# Revit family: RN 90046 Optifitt-Serra-Nippel doppio ridotto
name_source: partatom
category: Rohrformteile
units: mm (PartAtom-declared; Revit-internal decimal feet)

## family parameters
Arbeitsebenenbasiert = Nein
Beim Laden mit Abzugskörper schneiden = Nein
Bemaßung runder Anschluss = Durchmesser verwenden
Gemeinsam genutzt = Nein
Immer vertikal = Ja
Teiletyp = Nicht definiert

## types (10) — shared parameters
1.010.00.2 Blattnummer der Richtlinie = 29
1.010.00.3 Ausgabedatum (Monat) der Richtlinie = 201308
1.010.00.4 Herstellername = R. Nussbaum AG
1.010.00.5 Revisionsdatum der Datei = 20190521
1.010.00.6 Webadresse des Herstellers = http://www.nussbaum.ch
1.100.00.4 Produktbezeichnung = Versorgung
1.110.00.2 Index = 3
1.110.00.4 Produktbezeichnung = Optifitt-Serra
1.960/3L.00.8 Link (URL) = https://www.nussbaum.ch
29.700.00.4 Produktname = Optifitt-Serra-Doppelnippel reduziert, für flachdichtende Verschraubungen
29.700.00.5 Produktkennung = 2
29.700.00.6 Querschnittsform = 1
29.700.00.7 Nennweitensystem = DN
29.700.00.8 Nenndrucksystem = PN
29.710.02.4 Nenndruck = 16
29.710.02.5 max. zul. Überdruck [hPa] = 1600
29.710.02.7 max. zul. Dauer-Betriebsdruck [hPa] = 1600
29.710.02.9 max. zul. Dauer-Betriebstemperatur [°C] = 90
Connector Visibility = Nein
EnclosingSpace Visibility = Nein
Hersteller = R. Nussbaum AG
URL = https://www.nussbaum.ch

## per-type parameters (varying)
- DN=12x15: 1.800.00.3 TGA-Nummer=01900300000000000000000000000000000000000000000026000000000000000010; 1.800.00.4 Kommentarfeld=90046.20, Optifitt-Serra-Doppelnippel reduziert, für flachdichtende Verschraubungen, DN=12x15, L=25, R=3/8; 1.810.00.3 Hersteller-Bestellnummer=90046.2; 1.810.00.4 DATANORM-Nummer=90046.2; 1.810.00.6 GTIN-Nummer=7612945723567; 29.710.02.10 Formstück-Gewicht [kg]=0.044; 29.710.02.3 Benennung=Optifitt-Serra-Doppelnippel reduziert, für flachdichtende Verschraubungen, DN=12x15, L=25, R=3/8; CONNECTOR0_DIAMETER_dX_0r=10 mm  [stored 0.0328084 ft]; CONNECTOR0_dX_01=10 mm  [stored 0.0328084 ft]; CONNECTOR0_ref_dX=10 mm  [stored 0.0328084 ft]; CONNECTOR1_DIAMETER_dX_0r=15 mm; CONNECTOR1_dX_00=15 mm; CONNECTOR1_dX_01=24 mm; CONNECTOR1_ref_dX=15 mm; CONNECTOR1_ref_dX2=24 mm; Modell=90046.2; R. Nussbaum AG 90046.20 de Visibility=Ja; R. Nussbaum AG 90046.21 de Visibility=Nein; R. Nussbaum AG 90046.22 de Visibility=Nein; R. Nussbaum AG 90046.23 de Visibility=Nein; R. Nussbaum AG 90046.24 de Visibility=Nein; R. Nussbaum AG 90046.25 de Visibility=Nein; R. Nussbaum AG 90046.26 de Visibility=Nein; R. Nussbaum AG 90046.27 de Visibility=Nein; R. Nussbaum AG 90046.29 de Visibility=Nein; R. Nussbaum AG 90046.31 de Visibility=Nein; Typenkommentare=Optifitt-Serra-Nippel doppio ridotto  DN=12x15
- DN=40x50: 1.800.00.3 TGA-Nummer=01900300000000000000000000000000000000000000000026000000000000000009; 1.800.00.4 Kommentarfeld=90046.31, Optifitt-Serra-Doppelnippel reduziert, für flachdichtende Verschraubungen, DN=40x50, L=49, R=1½; 1.810.00.3 Hersteller-Bestellnummer=90046.31; 1.810.00.4 DATANORM-Nummer=90046.31; 1.810.00.6 GTIN-Nummer=7612945723604; 29.710.02.10 Formstück-Gewicht [kg]=0.424; 29.710.02.3 Benennung=Optifitt-Serra-Doppelnippel reduziert, für flachdichtende Verschraubungen, DN=40x50, L=49, R=1½; CONNECTOR0_DIAMETER_dX_0r=40 mm; CONNECTOR0_dX_01=19 mm; CONNECTOR0_ref_dX=19 mm; CONNECTOR1_DIAMETER_dX_0r=50 mm; CONNECTOR1_dX_00=33 mm; CONNECTOR1_dX_01=49 mm; CONNECTOR1_ref_dX=33 mm; CONNECTOR1_ref_dX2=49 mm; Modell=90046.31; R. Nussbaum AG 90046.20 de Visibility=Nein; R. Nussbaum AG 90046.21 de Visibility=Nein; R. Nussbaum AG 90046.22 de Visibility=Nein; R. Nussbaum AG 90046.23 de Visibility=Nein; R. Nussbaum AG 90046.24 de Visibility=Nein; R. Nussbaum AG 90046.25 de Visibility=Nein; R. Nussbaum AG 90046.26 de Visibility=Nein; R. Nussbaum AG 90046.27 de Visibility=Nein; R. Nussbaum AG 90046.29 de Visibility=Nein; R. Nussbaum AG 90046.31 de Visibility=Ja; Typenkommentare=Optifitt-Serra-Nippel doppio ridotto  DN=40x50
- DN=15x25: 1.800.00.3 TGA-Nummer=01900300000000000000000000000000000000000000000026000000000000000008; 1.800.00.4 Kommentarfeld=90046.29, Optifitt-Serra-Doppelnippel reduziert, für flachdichtende Verschraubungen, DN=15x25, L=30, R=½; 1.810.00.3 Hersteller-Bestellnummer=90046.29; 1.810.00.4 DATANORM-Nummer=90046.29; 1.810.00.6 GTIN-Nummer=7612945723581; 29.710.02.10 Formstück-Gewicht [kg]=0.084; 29.710.02.3 Benennung=Optifitt-Serra-Doppelnippel reduziert, für flachdichtende Verschraubungen, DN=15x25, L=30, R=½; CONNECTOR0_DIAMETER_dX_0r=15 mm; CONNECTOR0_dX_01=13 mm; CONNECTOR0_ref_dX=13 mm; CONNECTOR1_DIAMETER_dX_0r=25 mm  [stored 0.082021 ft]; CONNECTOR1_dX_00=18 mm; CONNECTOR1_dX_01=30 mm; CONNECTOR1_ref_dX=18 mm; CONNECTOR1_ref_dX2=30 mm; Modell=90046.29; R. Nussbaum AG 90046.20 de Visibility=Nein; R. Nussbaum AG 90046.21 de Visibility=Nein; R. Nussbaum AG 90046.22 de Visibility=Nein; R. Nussbaum AG 90046.23 de Visibility=Nein; R. Nussbaum AG 90046.24 de Visibility=Nein; R. Nussbaum AG 90046.25 de Visibility=Nein; R. Nussbaum AG 90046.26 de Visibility=Nein; R. Nussbaum AG 90046.27 de Visibility=Nein; R. Nussbaum AG 90046.29 de Visibility=Ja; R. Nussbaum AG 90046.31 de Visibility=Nein; Typenkommentare=Optifitt-Serra-Nippel doppio ridotto  DN=15x25
- DN=25: 1.800.00.3 TGA-Nummer=01900300000000000000000000000000000000000000000026000000000000000007; 1.800.00.4 Kommentarfeld=90046.27, Optifitt-Serra-Doppelnippel reduziert, für flachdichtende Verschraubungen, DN=25, L=39, R=1; 1.810.00.3 Hersteller-Bestellnummer=90046.27; 1.810.00.4 DATANORM-Nummer=90046.27; 1.810.00.6 GTIN-Nummer=7612945035219; 29.710.02.10 Formstück-Gewicht [kg]=0.095; 29.710.02.3 Benennung=Optifitt-Serra-Doppelnippel reduziert, für flachdichtende Verschraubungen, DN=25, L=39, R=1; CONNECTOR0_DIAMETER_dX_0r=25 mm  [stored 0.082021 ft]; CONNECTOR0_dX_01=17 mm; CONNECTOR0_ref_dX=17 mm; CONNECTOR1_DIAMETER_dX_0r=25 mm  [stored 0.082021 ft]; CONNECTOR1_dX_00=24 mm; CONNECTOR1_dX_01=36 mm; CONNECTOR1_ref_dX=24 mm; CONNECTOR1_ref_dX2=36 mm; Modell=90046.27; R. Nussbaum AG 90046.20 de Visibility=Nein; R. Nussbaum AG 90046.21 de Visibility=Nein; R. Nussbaum AG 90046.22 de Visibility=Nein; R. Nussbaum AG 90046.23 de Visibility=Nein; R. Nussbaum AG 90046.24 de Visibility=Nein; R. Nussbaum AG 90046.25 de Visibility=Nein; R. Nussbaum AG 90046.26 de Visibility=Nein; R. Nussbaum AG 90046.27 de Visibility=Ja; R. Nussbaum AG 90046.29 de Visibility=Nein; R. Nussbaum AG 90046.31 de Visibility=Nein; Typenkommentare=Optifitt-Serra-Nippel doppio ridotto  DN=25
- DN=20: 1.800.00.3 TGA-Nummer=01900300000000000000000000000000000000000000000026000000000000000006; 1.800.00.4 Kommentarfeld=90046.26, Optifitt-Serra-Doppelnippel reduziert, für flachdichtende Verschraubungen, DN=20, L=33, R=¾; 1.810.00.3 Hersteller-Bestellnummer=90046.26; 1.810.00.4 DATANORM-Nummer=90046.26; 1.810.00.6 GTIN-Nummer=7612945035202; 29.710.02.10 Formstück-Gewicht [kg]=0.059; 29.710.02.3 Benennung=Optifitt-Serra-Doppelnippel reduziert, für flachdichtende Verschraubungen, DN=20, L=33, R=¾; CONNECTOR0_DIAMETER_dX_0r=20 mm; CONNECTOR0_dX_01=15 mm; CONNECTOR0_ref_dX=15 mm; CONNECTOR1_DIAMETER_dX_0r=20 mm; CONNECTOR1_dX_00=21 mm; CONNECTOR1_dX_01=33 mm; CONNECTOR1_ref_dX=21 mm; CONNECTOR1_ref_dX2=33 mm; Modell=90046.26; R. Nussbaum AG 90046.20 de Visibility=Nein; R. Nussbaum AG 90046.21 de Visibility=Nein; R. Nussbaum AG 90046.22 de Visibility=Nein; R. Nussbaum AG 90046.23 de Visibility=Nein; R. Nussbaum AG 90046.24 de Visibility=Nein; R. Nussbaum AG 90046.25 de Visibility=Nein; R. Nussbaum AG 90046.26 de Visibility=Ja; R. Nussbaum AG 90046.27 de Visibility=Nein; R. Nussbaum AG 90046.29 de Visibility=Nein; R. Nussbaum AG 90046.31 de Visibility=Nein; Typenkommentare=Optifitt-Serra-Nippel doppio ridotto  DN=20
- DN=32x40: 1.800.00.3 TGA-Nummer=01900300000000000000000000000000000000000000000026000000000000000005; 1.800.00.4 Kommentarfeld=90046.25, Optifitt-Serra-Doppelnippel reduziert, für flachdichtende Verschraubungen, DN=32x40, L=45, R=1¼; 1.810.00.3 Hersteller-Bestellnummer=90046.25; 1.810.00.4 DATANORM-Nummer=90046.25; 1.810.00.6 GTIN-Nummer=7612945035196; 29.710.02.10 Formstück-Gewicht [kg]=0.214; 29.710.02.3 Benennung=Optifitt-Serra-Doppelnippel reduziert, für flachdichtende Verschraubungen, DN=32x40, L=45, R=1¼; CONNECTOR0_DIAMETER_dX_0r=32 mm; CONNECTOR0_dX_01=19 mm; CONNECTOR0_ref_dX=19 mm; CONNECTOR1_DIAMETER_dX_0r=40 mm; CONNECTOR1_dX_00=31 mm; CONNECTOR1_dX_01=45 mm; CONNECTOR1_ref_dX=31 mm; CONNECTOR1_ref_dX2=45 mm; Modell=90046.25; R. Nussbaum AG 90046.20 de Visibility=Nein; R. Nussbaum AG 90046.21 de Visibility=Nein; R. Nussbaum AG 90046.22 de Visibility=Nein; R. Nussbaum AG 90046.23 de Visibility=Nein; R. Nussbaum AG 90046.24 de Visibility=Nein; R. Nussbaum AG 90046.25 de Visibility=Ja; R. Nussbaum AG 90046.26 de Visibility=Nein; R. Nussbaum AG 90046.27 de Visibility=Nein; R. Nussbaum AG 90046.29 de Visibility=Nein; R. Nussbaum AG 90046.31 de Visibility=Nein; Typenkommentare=Optifitt-Serra-Nippel doppio ridotto  DN=32x40
- DN=25x32: 1.800.00.3 TGA-Nummer=01900300000000000000000000000000000000000000000026000000000000000004; 1.800.00.4 Kommentarfeld=90046.24, Optifitt-Serra-Doppelnippel reduziert, für flachdichtende Verschraubungen, DN=25x32, L=37, R=1; 1.810.00.3 Hersteller-Bestellnummer=90046.24; 1.810.00.4 DATANORM-Nummer=90046.24; 1.810.00.6 GTIN-Nummer=7612945035189; 29.710.02.10 Formstück-Gewicht [kg]=0.135; 29.710.02.3 Benennung=Optifitt-Serra-Doppelnippel reduziert, für flachdichtende Verschraubungen, DN=25x32, L=37, R=1; CONNECTOR0_DIAMETER_dX_0r=25 mm  [stored 0.082021 ft]; CONNECTOR0_dX_01=17 mm; CONNECTOR0_ref_dX=17 mm; CONNECTOR1_DIAMETER_dX_0r=32 mm; CONNECTOR1_dX_00=22 mm; CONNECTOR1_dX_01=36 mm; CONNECTOR1_ref_dX=22 mm; CONNECTOR1_ref_dX2=36 mm; Modell=90046.24; R. Nussbaum AG 90046.20 de Visibility=Nein; R. Nussbaum AG 90046.21 de Visibility=Nein; R. Nussbaum AG 90046.22 de Visibility=Nein; R. Nussbaum AG 90046.23 de Visibility=Nein; R. Nussbaum AG 90046.24 de Visibility=Ja; R. Nussbaum AG 90046.25 de Visibility=Nein; R. Nussbaum AG 90046.26 de Visibility=Nein; R. Nussbaum AG 90046.27 de Visibility=Nein; R. Nussbaum AG 90046.29 de Visibility=Nein; R. Nussbaum AG 90046.31 de Visibility=Nein; Typenkommentare=Optifitt-Serra-Nippel doppio ridotto  DN=25x32
- DN=20x25: 1.800.00.3 TGA-Nummer=01900300000000000000000000000000000000000000000026000000000000000003; 1.800.00.4 Kommentarfeld=90046.23, Optifitt-Serra-Doppelnippel reduziert, für flachdichtende Verschraubungen, DN=20x25, L=35, R=¾; 1.810.00.3 Hersteller-Bestellnummer=90046.23; 1.810.00.4 DATANORM-Nummer=90046.23; 1.810.00.6 GTIN-Nummer=7612945035172; 29.710.02.10 Formstück-Gewicht [kg]=0.089; 29.710.02.3 Benennung=Optifitt-Serra-Doppelnippel reduziert, für flachdichtende Verschraubungen, DN=20x25, L=35, R=¾; CONNECTOR0_DIAMETER_dX_0r=20 mm; CONNECTOR0_dX_01=15 mm; CONNECTOR0_ref_dX=15 mm; CONNECTOR1_DIAMETER_dX_0r=25 mm  [stored 0.082021 ft]; CONNECTOR1_dX_00=21 mm; CONNECTOR1_dX_01=35 mm; CONNECTOR1_ref_dX=21 mm; CONNECTOR1_ref_dX2=35 mm; Modell=90046.23; R. Nussbaum AG 90046.20 de Visibility=Nein; R. Nussbaum AG 90046.21 de Visibility=Nein; R. Nussbaum AG 90046.22 de Visibility=Nein; R. Nussbaum AG 90046.23 de Visibility=Ja; R. Nussbaum AG 90046.24 de Visibility=Nein; R. Nussbaum AG 90046.25 de Visibility=Nein; R. Nussbaum AG 90046.26 de Visibility=Nein; R. Nussbaum AG 90046.27 de Visibility=Nein; R. Nussbaum AG 90046.29 de Visibility=Nein; R. Nussbaum AG 90046.31 de Visibility=Nein; Typenkommentare=Optifitt-Serra-Nippel doppio ridotto  DN=20x25
- DN=15x20: 1.800.00.3 TGA-Nummer=01900300000000000000000000000000000000000000000026000000000000000002; 1.800.00.4 Kommentarfeld=90046.22, Optifitt-Serra-Doppelnippel reduziert, für flachdichtende Verschraubungen, DN=15x20, L=30, R=½; 1.810.00.3 Hersteller-Bestellnummer=90046.22; 1.810.00.4 DATANORM-Nummer=90046.22; 1.810.00.6 GTIN-Nummer=7612945035165; 29.710.02.10 Formstück-Gewicht [kg]=0.052; 29.710.02.3 Benennung=Optifitt-Serra-Doppelnippel reduziert, für flachdichtende Verschraubungen, DN=15x20, L=30, R=½; CONNECTOR0_DIAMETER_dX_0r=15 mm; CONNECTOR0_dX_01=13 mm; CONNECTOR0_ref_dX=13 mm; CONNECTOR1_DIAMETER_dX_0r=20 mm; CONNECTOR1_dX_00=19 mm; CONNECTOR1_dX_01=31 mm; CONNECTOR1_ref_dX=19 mm; CONNECTOR1_ref_dX2=31 mm; Modell=90046.22; R. Nussbaum AG 90046.20 de Visibility=Nein; R. Nussbaum AG 90046.21 de Visibility=Nein; R. Nussbaum AG 90046.22 de Visibility=Ja; R. Nussbaum AG 90046.23 de Visibility=Nein; R. Nussbaum AG 90046.24 de Visibility=Nein; R. Nussbaum AG 90046.25 de Visibility=Nein; R. Nussbaum AG 90046.26 de Visibility=Nein; R. Nussbaum AG 90046.27 de Visibility=Nein; R. Nussbaum AG 90046.29 de Visibility=Nein; R. Nussbaum AG 90046.31 de Visibility=Nein; Typenkommentare=Optifitt-Serra-Nippel doppio ridotto  DN=15x20
- DN=12x20: 1.800.00.3 TGA-Nummer=01900300000000000000000000000000000000000000000026000000000000000001; 1.800.00.4 Kommentarfeld=90046.21, Optifitt-Serra-Doppelnippel reduziert, für flachdichtende Verschraubungen, DN=12x20, L=27, R=3/8; 1.810.00.3 Hersteller-Bestellnummer=90046.21; 1.810.00.4 DATANORM-Nummer=90046.21; 1.810.00.6 GTIN-Nummer=7612945035158; 29.710.02.10 Formstück-Gewicht [kg]=0.046; 29.710.02.3 Benennung=Optifitt-Serra-Doppelnippel reduziert, für flachdichtende Verschraubungen, DN=12x20, L=27, R=3/8; CONNECTOR0_DIAMETER_dX_0r=10 mm  [stored 0.0328084 ft]; CONNECTOR0_dX_01=10 mm  [stored 0.0328084 ft]; CONNECTOR0_ref_dX=10 mm  [stored 0.0328084 ft]; CONNECTOR1_DIAMETER_dX_0r=20 mm; CONNECTOR1_dX_00=16 mm; CONNECTOR1_dX_01=28 mm; CONNECTOR1_ref_dX=16 mm; CONNECTOR1_ref_dX2=28 mm; Modell=90046.21; R. Nussbaum AG 90046.20 de Visibility=Nein; R. Nussbaum AG 90046.21 de Visibility=Ja; R. Nussbaum AG 90046.22 de Visibility=Nein; R. Nussbaum AG 90046.23 de Visibility=Nein; R. Nussbaum AG 90046.24 de Visibility=Nein; R. Nussbaum AG 90046.25 de Visibility=Nein; R. Nussbaum AG 90046.26 de Visibility=Nein; R. Nussbaum AG 90046.27 de Visibility=Nein; R. Nussbaum AG 90046.29 de Visibility=Nein; R. Nussbaum AG 90046.31 de Visibility=Nein; Typenkommentare=Optifitt-Serra-Nippel doppio ridotto  DN=12x20

note: [stored X ft] marks values corroborated as IEEE doubles in the binary element streams (Revit-internal decimal feet)

## geometry (parser evidence)
native form markers: Sweep x1
no freeform markers — native parametric forms only
